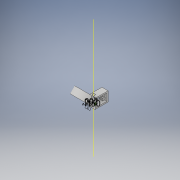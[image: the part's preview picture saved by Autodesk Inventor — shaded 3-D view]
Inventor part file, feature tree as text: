
AUTODESK INVENTOR PART (.ipt)
format: ipt  version: 2018 (Build 220112000, 112)  size: 276,480 bytes
history: native  units: in
note: dims shown in document units (in); Inventor stores cm internally (conversion verified against a paired STEP export)
features: sketch x12, extrude x9, plane x4, other x2
ambient origin geometry x8: Origin, YZ Plane, XZ Plane, XY Plane, X Axis, Y Axis, Z Axis, Center Point
bodies: Solid1 (feature_tree)
feature tree (27):
  extrude  "Extrusion1"  Depth=0.1in TaperAngle=0.0deg
  extrude  "Extrusion2"  Depth=0.75in
  plane  "Work Plane1"
  sketch  "Sketch3"  dims[d5=0.75in d6=0.0in d12=0.285in d13=0.0in]
  sketch  "Sketch4"  dims[d14=0.1in d15=-0.0206in d16=90.0deg]
  sketch  "Sketch5"  dims[d17=0.4in d18=0.0in d19=0.1in d20=0.0in d21=1.45in]
  sketch  "Sketch6"  dims[d22=1.275in]
  extrude  "Extrusion4"  Depth=0.75in TaperAngle=0.0deg
  other  "Work Axis1"
  plane  "Work Plane2"
  extrude  "Extrusion5"  TaperAngle=90.0deg  [1 undecoded]
  other  "Work Axis2"
  plane  "Work Plane3"
  sketch  "Sketch14"  dims[d65=0.25in d66=0.15in]
  extrude  "Extrusion7"  Depth=0.1in TaperAngle=0.0deg
  plane  "Work Plane5"
  extrude  "Extrusion10"  Depth=0.15in
  extrude  "Extrusion12"  Depth=0.15in
  extrude  "Extrusion13"  Depth=0.125in
  extrude  "Extrusion14"  Depth=0.1in
  sketch  "Sketch1"  dims[d0=0.4in d1=0.1in d2=0.0in]
  sketch  "Sketch2"  dims[d3=0.47in d4=0.75in]
  sketch  "Sketch7"  dims[d34=90.0deg d44=0.25in d45=0.0in d46=0.15in d47=0.0in d64=0.0022in]
  sketch  "Sketch18"  dims[d82=0.125in d83=0.125in]
  sketch  "Sketch20"  dims[d84=0.125in d85=0.1in]
  sketch  "Sketch21"  dims[d86=0.1in]
  sketch  "Sketch22"  dims[d87=0.1in d88=0.1in d89=1.0in d90=0.0in d96=-0.15in d97=0.11in d98=0.0in d99=0.185in d102=0.25in d103=0.19in d104=0.25in d105=0.045in d106=0.12in d107=0.0in d108=1.375in d109=1.275in d110=0.22in d111=0.1867in d112=0.187in d113=0.05in d114=0.05in d115=0.125in d116=0.125in d117=0.22in d118=0.2in d119=0.0in d120=0.5in d121=0.0in d48=1.0in d49=1.0in]
note: 1 required parameter value undecoded (feature->parameter linkage not recoverable at this tier; creation-order binding heuristic only, values carry confidence <= 0.55)
